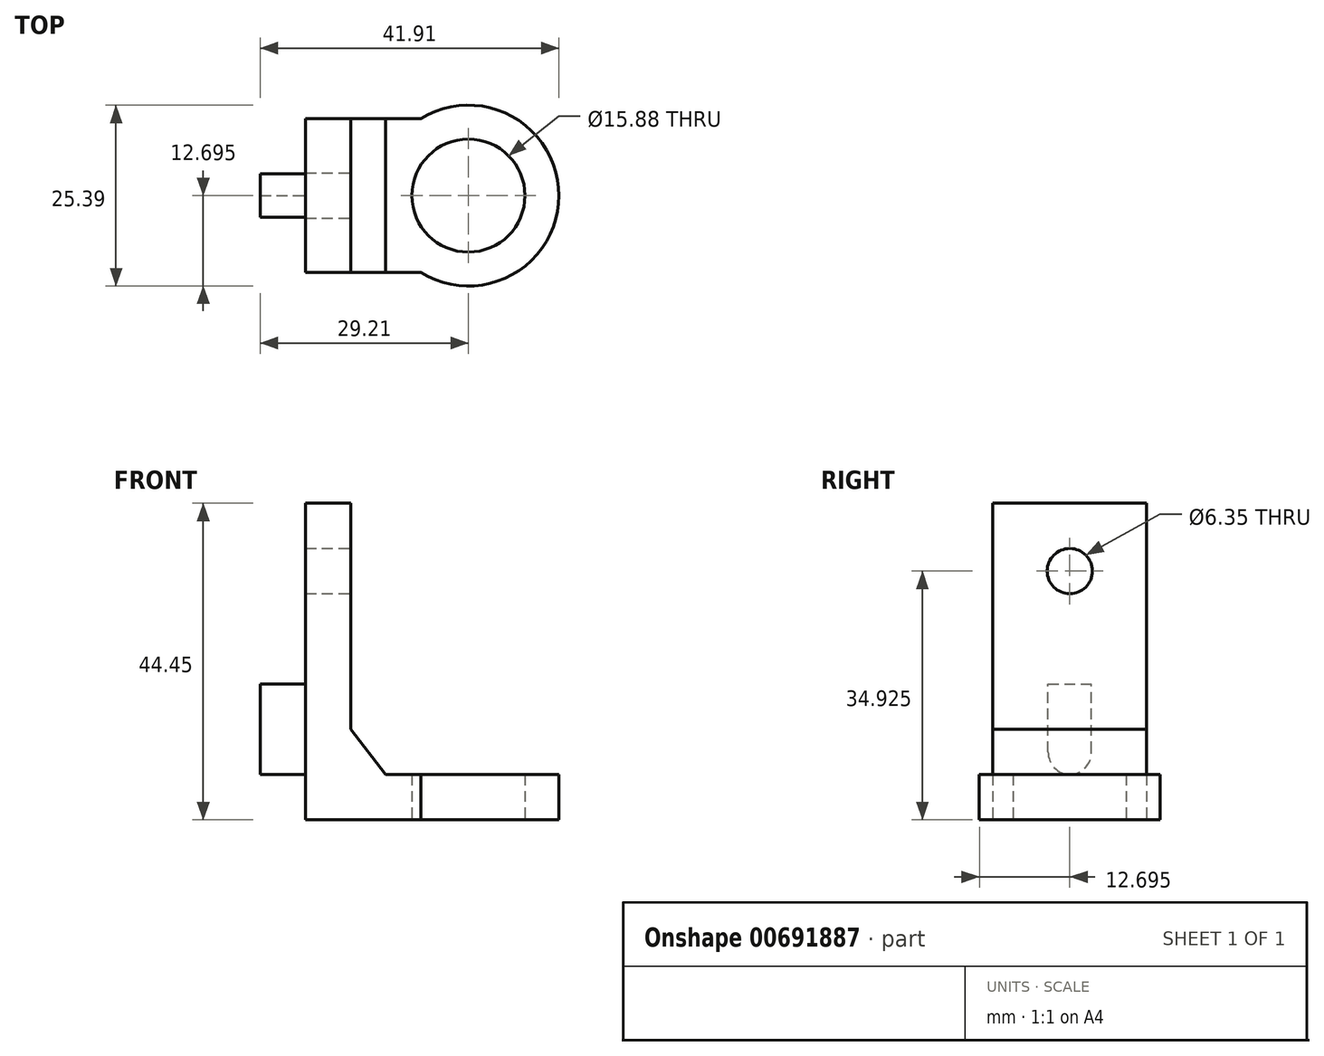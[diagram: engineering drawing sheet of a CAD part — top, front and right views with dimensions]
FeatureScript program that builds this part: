
annotation { "Feature Type Name" : "Feature", "Feature Type Description" : "" }
export const myFeature = defineFeature(function(context is Context, id is Id, definition is map)
    precondition{}
    {
        {
            var Q0;
            Q0=qCreatedBy(makeId("Top.planeOp"),FACE);
            var sketch = newSketch(context, id + "F0", { "sketchPlane" : qUnion([Q0])});
            skLineSegment(sketch, "E0.bottom", {"start": v(0, 0) * mm, "end": v(6.35, 0) * mm});
            skLineSegment(sketch, "E0.top", {"start": v(0, 21.6) * mm, "end": v(6.35, 21.6) * mm});
            skLineSegment(sketch, "E0.left", {"start": v(0, 0) * mm, "end": v(0, 21.6) * mm});
            skLineSegment(sketch, "E0.right", {"start": v(6.35, 0) * mm, "end": v(6.35, 21.59) * mm});
            skLineSegment(sketch, "E1.bottom", {"start": v(6.35, 0) * mm, "end": v(22.86, 0) * mm});
            skLineSegment(sketch, "E1.top", {"start": v(6.35, 21.6) * mm, "end": v(22.86, 21.6) * mm});
            skLineSegment(sketch, "E1.right", {"start": v(22.86, 0) * mm, "end": v(22.86, 21.59) * mm});
            skCircle(sketch, "E2", {"center": v(22.86, 10.8) * mm, "radius": 12.7 * mm});
            skLineSegment(sketch, "E3", {"start": v(0, 10.8) * mm, "end": v(6.35, 10.8) * mm});
            skLineSegment(sketch, "E4", {"start": v(3.18, 10.8) * mm, "end": v(3.17, 21.6) * mm});
            skLineSegment(sketch, "E5", {"start": v(3.18, 10.8) * mm, "end": v(3.18, 0) * mm});
            skSolve(sketch);
        }
        {
            var Q0;
            {var subQ0=sQuery(id+"F0.wireOp",EDGE,"E1.right");Q0=makeQuery(id+"F0.imprint","IMPRINT",FACE,{"disambiguationData":[TD([[makeQuery(id+"F0.imprint","IMPRINT",EDGE,{"derivedFrom":subQ0}),-1.0]])]});}
            var Q1;
            {var subQ0=sQuery(id+"F0.wireOp",EDGE,"E1.right");Q1=makeQuery(id+"F0.imprint","IMPRINT",FACE,{"disambiguationData":[TD([[makeQuery(id+"F0.imprint","IMPRINT",EDGE,{"derivedFrom":subQ0}),1.0]])]});}
            var Q2;
            {var subQ0=sQuery(id+"F0.wireOp",EDGE,"E0.right");Q2=makeQuery(id+"F0.imprint","IMPRINT",FACE,{"disambiguationData":[TD([[makeQuery(id+"F0.imprint","IMPRINT",EDGE,{"derivedFrom":subQ0}),-1.0]])]});}
            extrude(context, id + "F1", {"entities" : qUnion([Q0, Q1, Q2]), "depth" : 6.35 * mm, "offsetDistance" : 25.4 * mm});
        }
        {
            var Q0;
            Q0=makeQuery(id+"F0.imprint","IMPRINT",FACE,{"disambiguationData":[TD([[makeQuery(id+"F0.imprint","IMPRINT",EDGE,{"derivedFrom":sQuery(id+"F0.wireOp",EDGE,"E0.bottom")}),1.0]])]});
            var Q1;
            {var subQ3=sQuery(id+"F0.wireOp",EDGE,"E4");Q1=makeQuery(id+"F0.imprint","IMPRINT",FACE,{"disambiguationData":[TD([[makeQuery(id+"F0.imprint","IMPRINT",EDGE,{"derivedFrom":subQ3}),-1.0]])]});}
            var Q2;
            {var subQ3=sQuery(id+"F0.wireOp",EDGE,"E4");Q2=makeQuery(id+"F0.imprint","IMPRINT",FACE,{"disambiguationData":[TD([[makeQuery(id+"F0.imprint","IMPRINT",EDGE,{"derivedFrom":subQ3}),1.0]])]});}
            extrude(context, id + "F2", {"entities" : qUnion([Q0, Q1, Q2]), "operationType" : NewBodyOperationType.ADD, "depth" : 44.45 * mm, "offsetDistance" : 25.4 * mm});
        }
        {
            var Q0;
            Q0=sQuery(id+"F0.wireOp",VERTEX,"E2.center");
            var Q1;
            Q1=makeQuery(id+"F1.opExtrude","SWEPT_BODY",BODY,{"disambiguationData":[OSD([sQuery(id+"F0.wireOp",EDGE,"E1.bottom"),sQuery(id+"F0.wireOp",EDGE,"E1.top"),sQuery(id+"F0.wireOp",EDGE,"E0.right"),sQuery(id+"F0.wireOp",EDGE,"E2")])]});
            hole(context, id + "F3", {"style" : HoleStyle.SIMPLE, "endStyle" : HoleEndStyle.THROUGH, "oppositeDirection" : true, "holeDiameter" : 15.88 * mm, "majorDiameter" : 6.35 * mm, "isTappedThrough" : true, "tappedDepth" : 12.7 * mm, "tapClearance" : 3, "locations" : qUnion([Q0]), "scope" : qUnion([Q1])});
        }
        {
            var Q0;
            Q0=makeQuery(id+"F2.opExtrude","SWEPT_FACE",FACE,{"disambiguationData":[OSD([sQuery(id+"F0.wireOp",EDGE,"E0.right")])]});
            var sketch = newSketch(context, id + "F4", { "sketchPlane" : qUnion([Q0])});
            skLineSegment(sketch, "E6", {"start": v(10.8, 44.45) * mm, "end": v(10.8, 34.93) * mm});
            skLineSegment(sketch, "E7", {"start": v(10.8, 34.93) * mm, "end": v(10.8, 0) * mm});
            skLineSegment(sketch, "E8", {"start": v(10.8, 0) * mm, "end": v(10.8, 6.35) * mm});
            skLineSegment(sketch, "E9", {"start": v(10.8, 6.35) * mm, "end": v(10.8, 12.7) * mm});
            skLineSegment(sketch, "E10.bottom", {"start": v(13.84, 19.05) * mm, "end": v(7.75, 19.05) * mm});
            skLineSegment(sketch, "E10.top", {"start": v(13.84, 6.35) * mm, "end": v(7.75, 6.35) * mm});
            skLineSegment(sketch, "E10.left", {"start": v(13.84, 19.05) * mm, "end": v(13.84, 6.35) * mm});
            skLineSegment(sketch, "E10.right", {"start": v(7.75, 19.05) * mm, "end": v(7.75, 6.35) * mm});
            skPoint(sketch, "E10.middle", {"position": v(10.8, 12.7) * mm});
            skSolve(sketch);
        }
        {
            var Q0;
            Q0=sQuery(id+"F4.wireOp",VERTEX,"E6.end");
            var Q1;
            Q1=makeQuery(id+"F1.opExtrude","SWEPT_BODY",BODY,{"disambiguationData":[OSD([sQuery(id+"F0.wireOp",EDGE,"E1.bottom"),sQuery(id+"F0.wireOp",EDGE,"E1.top"),sQuery(id+"F0.wireOp",EDGE,"E0.right"),sQuery(id+"F0.wireOp",EDGE,"E2")])]});
            hole(context, id + "F5", {"style" : HoleStyle.SIMPLE, "endStyle" : HoleEndStyle.THROUGH, "holeDiameter" : 6.35 * mm, "majorDiameter" : 6.35 * mm, "isTappedThrough" : true, "tappedDepth" : 12.7 * mm, "tapClearance" : 3, "locations" : qUnion([Q0]), "scope" : qUnion([Q1])});
        }
        {
            var Q0;
            {var subQ0=sQuery(id+"F4.wireOp",EDGE,"E10.right");Q0=makeQuery(id+"F4.imprint","IMPRINT",FACE,{"disambiguationData":[TD([[makeQuery(id+"F4.imprint","IMPRINT",EDGE,{"derivedFrom":subQ0}),1.0]])]});}
            var Q1;
            {var subQ0=sQuery(id+"F4.wireOp",EDGE,"E10.left");Q1=makeQuery(id+"F4.imprint","IMPRINT",FACE,{"disambiguationData":[TD([[makeQuery(id+"F4.imprint","IMPRINT",EDGE,{"derivedFrom":subQ0}),-1.0]])]});}
            extrude(context, id + "F6", {"entities" : qUnion([Q0, Q1]), "operationType" : NewBodyOperationType.ADD, "oppositeDirection" : true, "depth" : 12.7 * mm, "offsetDistance" : 25.4 * mm});
        }
        {
            var Q0;
            Q0=makeQuery(id+"F6.opExtrude","SWEPT_EDGE",EDGE,{"disambiguationData":[OSD([sQuery(id+"F4.wireOp",EDGE,"E10.top"),sQuery(id+"F4.wireOp",EDGE,"E10.right")])]});
            var Q1;
            Q1=makeQuery(id+"F6.opExtrude","SWEPT_EDGE",EDGE,{"disambiguationData":[OSD([sQuery(id+"F4.wireOp",EDGE,"E10.top"),sQuery(id+"F4.wireOp",EDGE,"E10.left")])]});
            fillet(context, id + "F7", {"entities" : qUnion([Q0, Q1]), "radius" : 3.17 * mm, "tangentPropagation" : true, "allowEdgeOverflow" : false});
        }
        {
            var Q0;
            Q0=makeQuery(id+"F2.boolean.opBoolean","MERGE",FACE,{"derivedFrom":[makeQuery(id+"F1.opExtrude","SWEPT_FACE",FACE,{"disambiguationData":[OSD([sQuery(id+"F0.wireOp",EDGE,"E1.bottom")])]}),makeQuery(id+"F2.opExtrude","SWEPT_FACE",FACE,{"disambiguationData":[OSD([sQuery(id+"F0.wireOp",EDGE,"E0.bottom")])]})]});
            var sketch = newSketch(context, id + "F8", { "sketchPlane" : qUnion([Q0])});
            skLineSegment(sketch, "E11", {"start": v(6.35, 12.7) * mm, "end": v(11.26, 6.35) * mm});
            skLineSegment(sketch, "E12", {"start": v(11.26, 6.35) * mm, "end": v(6.35, 6.35) * mm});
            skSolve(sketch);
        }
        {
            var Q0;
            {var subQ0=sQuery(id+"F8.wireOp",EDGE,"E11");Q0=makeQuery(id+"F8.imprint","IMPRINT",FACE,{"disambiguationData":[TD([[makeQuery(id+"F8.imprint","IMPRINT",EDGE,{"derivedFrom":subQ0}),-1.0]])]});}
            extrude(context, id + "F9", {"entities" : qUnion([Q0]), "operationType" : NewBodyOperationType.ADD, "oppositeDirection" : true, "depth" : 21.59 * mm, "offsetDistance" : 25.4 * mm});
        }
    });
